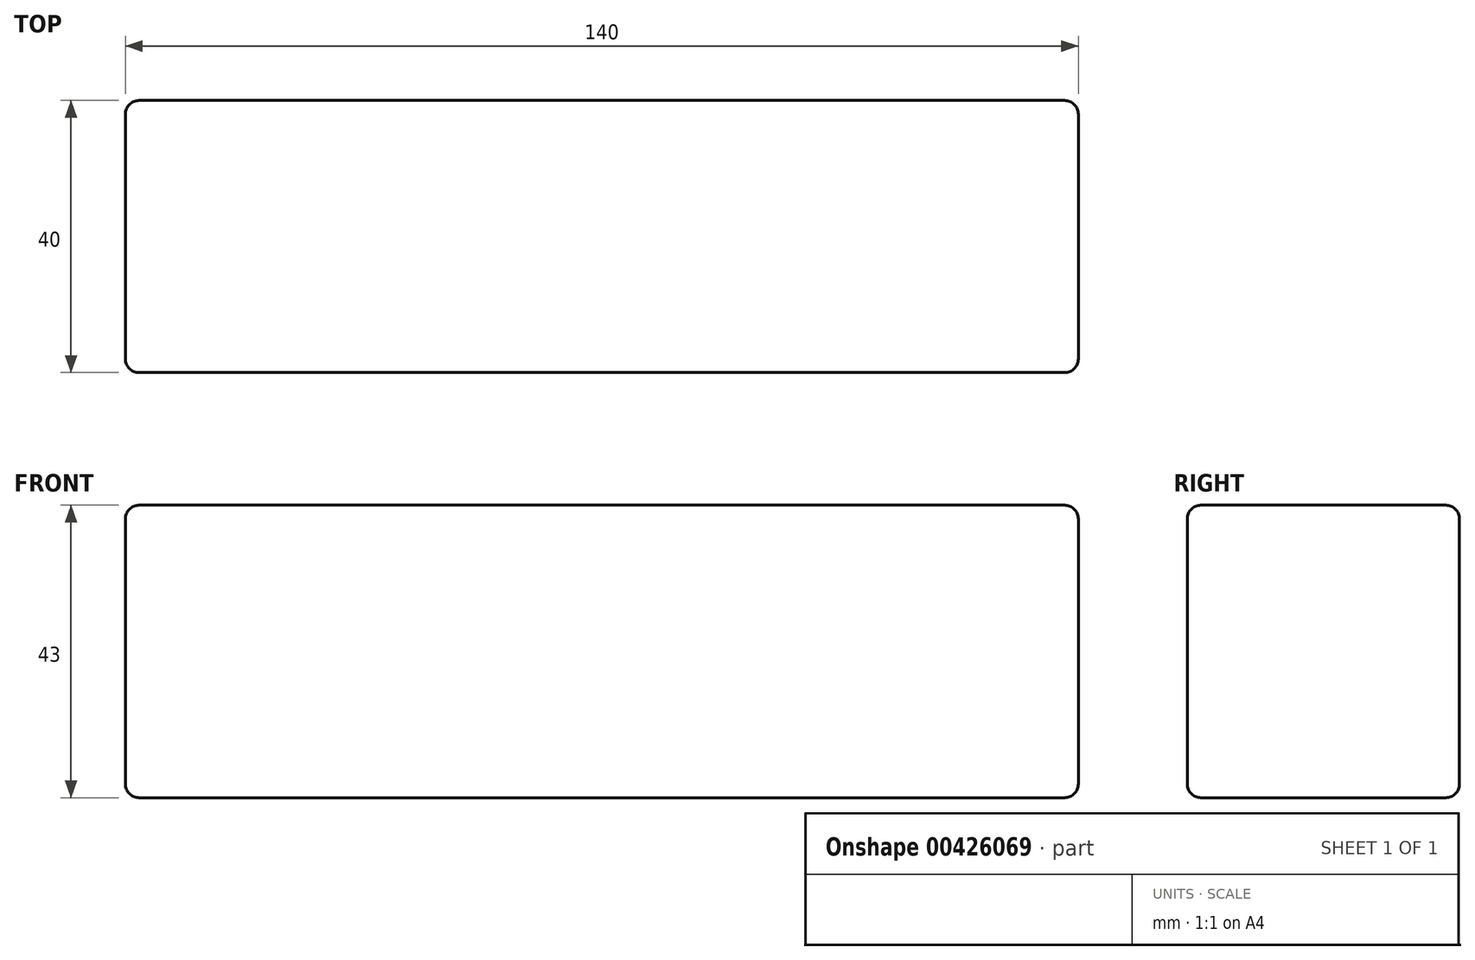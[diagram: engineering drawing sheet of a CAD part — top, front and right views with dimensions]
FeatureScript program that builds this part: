
annotation { "Feature Type Name" : "Feature", "Feature Type Description" : "" }
export const myFeature = defineFeature(function(context is Context, id is Id, definition is map)
    precondition{}
    {
        {
            var Q0;
            Q0=qCreatedBy(makeId("Top.planeOp"),FACE);
            var sketch = newSketch(context, id + "F0", { "sketchPlane" : qUnion([Q0])});
            skLineSegment(sketch, "E0.bottom", {"start": v(70, -20) * mm, "end": v(-70, -20) * mm});
            skLineSegment(sketch, "E0.top", {"start": v(70, 20) * mm, "end": v(-70, 20) * mm});
            skLineSegment(sketch, "E0.left", {"start": v(70, -20) * mm, "end": v(70, 20) * mm});
            skLineSegment(sketch, "E0.right", {"start": v(-70, -20) * mm, "end": v(-70, 20) * mm});
            skPoint(sketch, "E0.middle", {"position": v(0, 0) * mm});
            skSolve(sketch);
        }
        {
            var Q0;
            Q0=qSketchRegion(id+"F0",true);
            extrude(context, id + "F1", {"entities" : qUnion([Q0]), "depth" : 43 * mm});
        }
        {
            var Q0;
            Q0=makeQuery(id+"F1.opExtrude","SWEPT_FACE",FACE,{"disambiguationData":[OSD([sQuery(id+"F0.wireOp",EDGE,"E0.bottom")])]});
            var Q1;
            Q1=makeQuery(id+"F1.opExtrude","CAP_FACE",FACE,{"disambiguationData":[OSD([sQuery(id+"F0.wireOp",EDGE,"E0.bottom"),sQuery(id+"F0.wireOp",EDGE,"E0.top"),sQuery(id+"F0.wireOp",EDGE,"E0.left"),sQuery(id+"F0.wireOp",EDGE,"E0.right")])],"isStart":false});
            var Q2;
            Q2=makeQuery(id+"F1.opExtrude","SWEPT_FACE",FACE,{"disambiguationData":[OSD([sQuery(id+"F0.wireOp",EDGE,"E0.top")])]});
            var Q3;
            Q3=makeQuery(id+"F1.opExtrude","CAP_FACE",FACE,{"disambiguationData":[OSD([sQuery(id+"F0.wireOp",EDGE,"E0.bottom"),sQuery(id+"F0.wireOp",EDGE,"E0.top"),sQuery(id+"F0.wireOp",EDGE,"E0.left"),sQuery(id+"F0.wireOp",EDGE,"E0.right")])],"isStart":true});
            fillet(context, id + "F2", {"entities" : qUnion([Q0, Q1, Q2, Q3]), "radius" : 2 * mm, "tangentPropagation" : true, "allowEdgeOverflow" : false});
        }
    });
